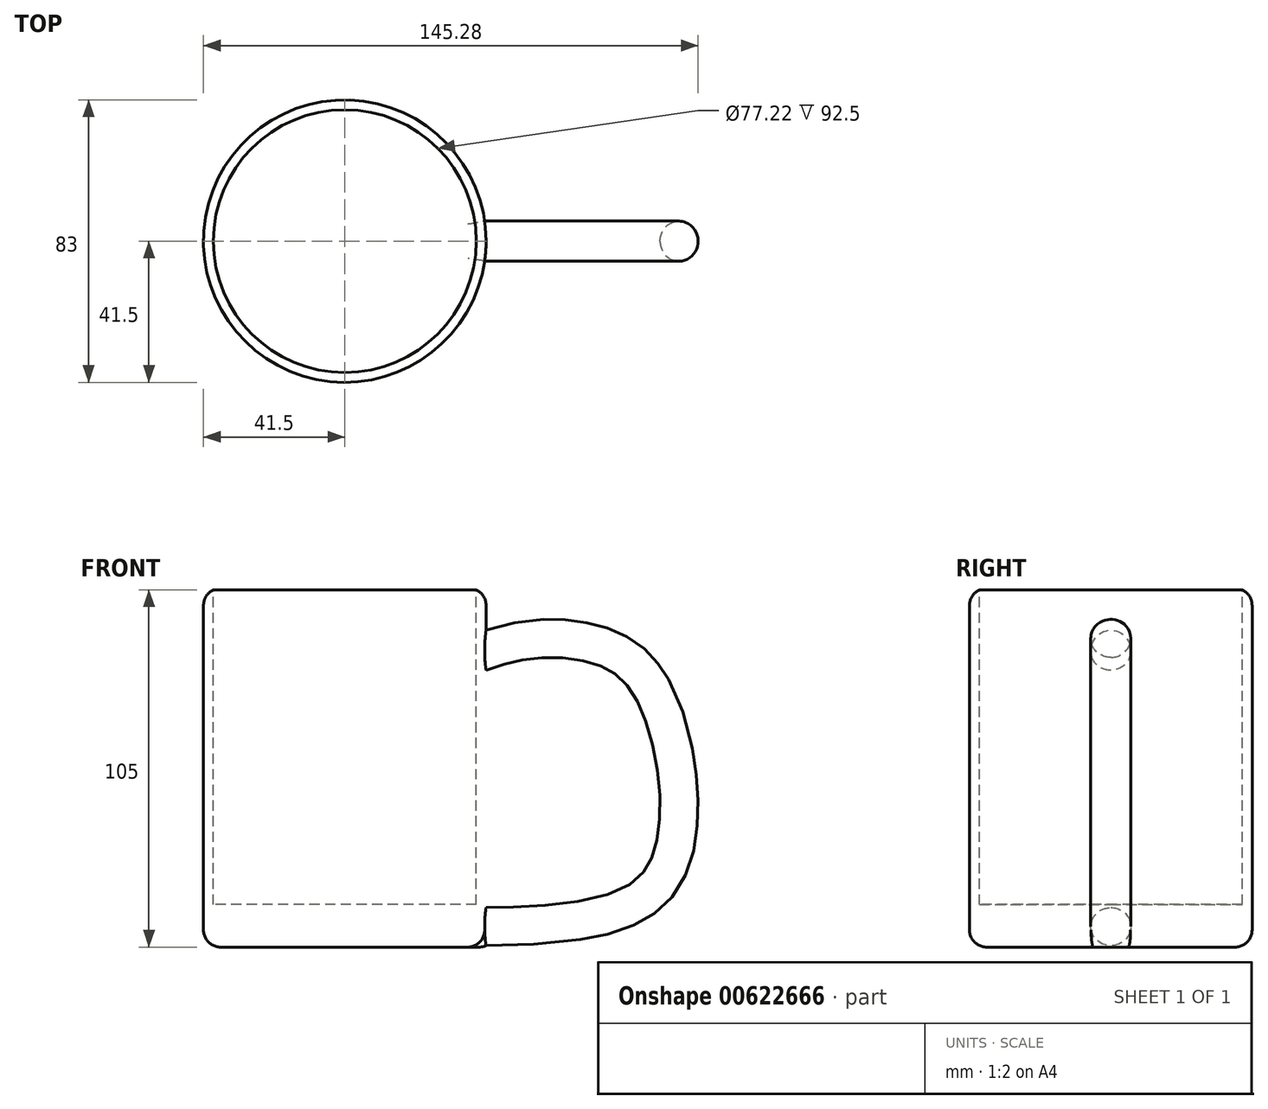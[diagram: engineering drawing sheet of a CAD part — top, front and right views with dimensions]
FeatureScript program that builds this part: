
annotation { "Feature Type Name" : "Feature", "Feature Type Description" : "" }
export const myFeature = defineFeature(function(context is Context, id is Id, definition is map)
    precondition{}
    {
        {
            var Q0;
            Q0=qCreatedBy(makeId("Top.planeOp"),FACE);
            var sketch = newSketch(context, id + "F0", { "sketchPlane" : qUnion([Q0])});
            skCircle(sketch, "E0", {"center": v(0, 0) * mm, "radius": 41.5 * mm});
            skSolve(sketch);
        }
        {
            var Q0;
            Q0=qSketchRegion(id+"F0",true);
            extrude(context, id + "F1", {"entities" : qUnion([Q0]), "depth" : 105 * mm, "offsetDistance" : 25 * mm});
        }
        {
            var Q0;
            Q0=qCreatedBy(makeId("Right.planeOp"),FACE);
            cPlane(context, id + "F2", {"entities" : qUnion([Q0]), "cplaneType" : CPlaneType.OFFSET, "offset" : 41.5 * mm, "width" : 150 * mm, "height" : 150 * mm});
        }
        {
            var Q0;
            Q0=qCreatedBy(makeId("Front.planeOp"),FACE);
            var sketch = newSketch(context, id + "F3", { "sketchPlane" : qUnion([Q0])});
            skFitSpline(sketch, "E1", {"points": [v(36.07, 86.13) * mm, v(56.56, 91.25) * mm, v(81.8, 86.13) * mm, v(95.2, 65.63) * mm, v(97.95, 30.94) * mm, v(81.8, 10.45) * mm, v(36.07, 5.32) * mm, v(29.37, 5.32) * mm], "startDerivative": vector(146.94, 51.71) * mm, "endDerivative": vector(-63.52, -0.33) * mm});
            skSolve(sketch);
        }
        {
            var Q0;
            Q0=qCreatedBy(id+"F2.planeOp",FACE);
            var sketch = newSketch(context, id + "F4", { "sketchPlane" : qUnion([Q0])});
            skCircle(sketch, "E2", {"center": v(0, 87.26) * mm, "radius": 5.89 * mm});
            skSolve(sketch);
        }
        {
            var Q0;
            Q0=qSketchRegion(id+"F4",true);
            var Q1;
            Q1=qConstructionFilter(qBodyType(qCreatedBy(id+"F3",EDGE),BodyType.WIRE),ConstructionObject.NO);
            sweep(context, id + "F5", {"operationType" : NewBodyOperationType.ADD, "profiles" : qUnion([Q0]), "path" : qUnion([Q1])});
        }
        {
            var Q0;
            Q0=makeQuery(id+"F1.opExtrude","CAP_FACE",FACE,{"disambiguationData":[OSD([sQuery(id+"F0.wireOp",EDGE,"E0")])],"isStart":false});
            var sketch = newSketch(context, id + "F6", { "sketchPlane" : qUnion([Q0])});
            skCircle(sketch, "E3", {"center": v(0, 0) * mm, "radius": 38.6 * mm});
            skSolve(sketch);
        }
        {
            var Q0;
            Q0=qSketchRegion(id+"F6",true);
            extrude(context, id + "F7", {"entities" : qUnion([Q0]), "operationType" : NewBodyOperationType.REMOVE, "oppositeDirection" : true, "depth" : 92.5 * mm, "offsetDistance" : 25 * mm});
        }
        {
            var Q0;
            Q0=makeQuery(id+"F1.opExtrude","CAP_EDGE",EDGE,{"disambiguationData":[OSD([sQuery(id+"F0.wireOp",EDGE,"E0")])],"isStart":false});
            var Q1;
            Q1=makeQuery(id+"F1.opExtrude","CAP_EDGE",EDGE,{"disambiguationData":[OSD([sQuery(id+"F0.wireOp",EDGE,"E0")])],"isStart":true});
            fillet(context, id + "F8", {"entities" : qUnion([Q0, Q1]), "radius" : 5 * mm, "tangentPropagation" : true, "allowEdgeOverflow" : false});
        }
    });
